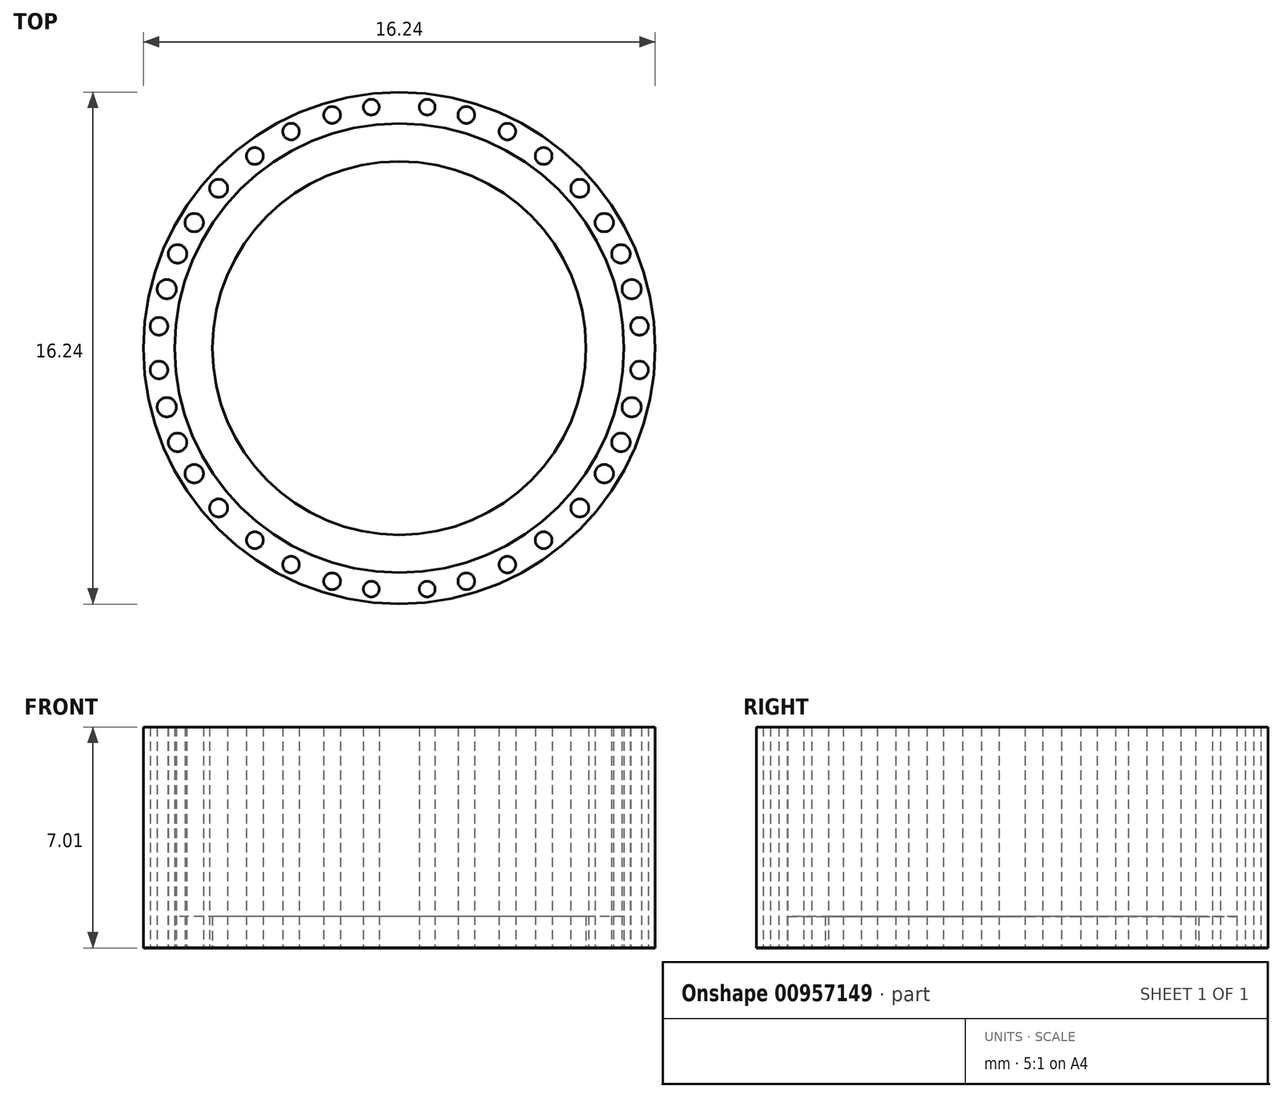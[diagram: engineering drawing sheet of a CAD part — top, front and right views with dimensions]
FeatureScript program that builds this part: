
annotation { "Feature Type Name" : "Feature", "Feature Type Description" : "" }
export const myFeature = defineFeature(function(context is Context, id is Id, definition is map)
    precondition{}
    {
        {
            var Q0;
            Q0=qCreatedBy(makeId("Top.planeOp"),FACE);
            var sketch = newSketch(context, id + "F0", { "sketchPlane" : qUnion([Q0])});
            skCircle(sketch, "E0.0", {"center": v(0, 0) * mm, "radius": 8.22 * mm});
            skCircle(sketch, "E1.0", {"center": v(0, 0) * mm, "radius": 8.12 * mm});
            skCircle(sketch, "E2.0", {"center": v(0, 0) * mm, "radius": 7.13 * mm});
            skCircle(sketch, "E3.0", {"center": v(0, 0) * mm, "radius": 9.1 * mm});
            skCircle(sketch, "E4.0", {"center": v(0, 0) * mm, "radius": 5.93 * mm});
            skSolve(sketch);
        }
        {
            var Q0;
            Q0=makeQuery(id+"F0.imprint","IMPRINT",FACE,{"disambiguationData":[TD([[makeQuery(id+"F0.imprint","IMPRINT",EDGE,{"derivedFrom":sQuery(id+"F0.wireOp",EDGE,"E1.0")}),1.0]])]});
            var Q1;
            Q1=sQuery(id+"F0.wireOp",EDGE,"E1.0");
            var Q2;
            Q2=sQuery(id+"F0.wireOp",EDGE,"E2.0");
            extrude(context, id + "F1", {"entities" : qUnion([Q0]), "surfaceEntities" : qUnion([Q1, Q2]), "depth" : 0.01 * mm, "offsetDistance" : 25 * mm});
        }
        {
            var Q0;
            Q0=makeQuery(id+"F0.imprint","IMPRINT",FACE,{"disambiguationData":[TD([[makeQuery(id+"F0.imprint","IMPRINT",EDGE,{"derivedFrom":sQuery(id+"F0.wireOp",EDGE,"E2.0")}),1.0]])]});
            extrude(context, id + "F2", {"entities" : qUnion([Q0]), "operationType" : NewBodyOperationType.ADD, "depth" : 1 * mm, "offsetDistance" : 25 * mm});
        }
        {
            var Q0;
            Q0=makeQuery(id+"F1.opExtrude","CAP_FACE",FACE,{"disambiguationData":[OSD([sQuery(id+"F0.wireOp",EDGE,"E1.0"),sQuery(id+"F0.wireOp",EDGE,"E2.0")])],"isStart":false});
            var sketch = newSketch(context, id + "F3", { "sketchPlane" : qUnion([Q0])});
            skCircle(sketch, "E5", {"center": v(-4.58, 6.1) * mm, "radius": 0.27 * mm});
            skCircle(sketch, "E6", {"center": v(-5.73, 5.07) * mm, "radius": 0.29 * mm});
            skCircle(sketch, "E7", {"center": v(-6.5, 3.98) * mm, "radius": 0.3 * mm});
            skCircle(sketch, "E8", {"center": v(-7.03, 3) * mm, "radius": 0.3 * mm});
            skCircle(sketch, "E9", {"center": v(-7.37, 1.87) * mm, "radius": 0.3 * mm});
            skCircle(sketch, "E10", {"center": v(-7.62, 0.7) * mm, "radius": 0.28 * mm});
            skCircle(sketch, "E11", {"center": v(-3.43, 6.87) * mm, "radius": 0.26 * mm});
            skCircle(sketch, "E12", {"center": v(-2.13, 7.4) * mm, "radius": 0.27 * mm});
            skCircle(sketch, "E13", {"center": v(-0.89, 7.65) * mm, "radius": 0.25 * mm});
            skCircle(sketch, "E14.MirrorC", {"center": v(6.5, 3.98) * mm, "radius": 0.3 * mm});
            skCircle(sketch, "E15.MirrorC", {"center": v(0.89, 7.65) * mm, "radius": 0.25 * mm});
            skCircle(sketch, "E16.MirrorC", {"center": v(7.03, 3) * mm, "radius": 0.3 * mm});
            skCircle(sketch, "E17.MirrorC", {"center": v(7.62, 0.7) * mm, "radius": 0.28 * mm});
            skCircle(sketch, "E18.MirrorC", {"center": v(7.37, 1.87) * mm, "radius": 0.3 * mm});
            skCircle(sketch, "E19.MirrorC", {"center": v(5.73, 5.07) * mm, "radius": 0.29 * mm});
            skCircle(sketch, "E20.MirrorC", {"center": v(4.58, 6.1) * mm, "radius": 0.27 * mm});
            skCircle(sketch, "E21.MirrorC", {"center": v(3.43, 6.87) * mm, "radius": 0.26 * mm});
            skCircle(sketch, "E22.MirrorC", {"center": v(2.13, 7.4) * mm, "radius": 0.27 * mm});
            skCircle(sketch, "E23.MirrorC", {"center": v(3.43, -6.87) * mm, "radius": 0.26 * mm});
            skCircle(sketch, "E24.MirrorC", {"center": v(2.13, -7.4) * mm, "radius": 0.27 * mm});
            skCircle(sketch, "E25.MirrorC", {"center": v(7.62, -0.7) * mm, "radius": 0.28 * mm});
            skCircle(sketch, "E26.MirrorC", {"center": v(-0.89, -7.65) * mm, "radius": 0.25 * mm});
            skCircle(sketch, "E27.MirrorC", {"center": v(7.37, -1.87) * mm, "radius": 0.3 * mm});
            skCircle(sketch, "E28.MirrorC", {"center": v(0.89, -7.65) * mm, "radius": 0.25 * mm});
            skCircle(sketch, "E29.MirrorC", {"center": v(6.5, -3.98) * mm, "radius": 0.3 * mm});
            skCircle(sketch, "E30.MirrorC", {"center": v(-4.58, -6.1) * mm, "radius": 0.27 * mm});
            skCircle(sketch, "E31.MirrorC", {"center": v(-7.37, -1.87) * mm, "radius": 0.3 * mm});
            skCircle(sketch, "E32.MirrorC", {"center": v(-7.62, -0.7) * mm, "radius": 0.28 * mm});
            skCircle(sketch, "E33.MirrorC", {"center": v(4.58, -6.1) * mm, "radius": 0.27 * mm});
            skCircle(sketch, "E34.MirrorC", {"center": v(-2.13, -7.4) * mm, "radius": 0.27 * mm});
            skCircle(sketch, "E35.MirrorC", {"center": v(-3.43, -6.87) * mm, "radius": 0.26 * mm});
            skCircle(sketch, "E36.MirrorC", {"center": v(5.73, -5.07) * mm, "radius": 0.29 * mm});
            skCircle(sketch, "E37.MirrorC", {"center": v(-5.73, -5.07) * mm, "radius": 0.29 * mm});
            skCircle(sketch, "E38.MirrorC", {"center": v(7.03, -3) * mm, "radius": 0.3 * mm});
            skCircle(sketch, "E39.MirrorC", {"center": v(-6.5, -3.98) * mm, "radius": 0.3 * mm});
            skCircle(sketch, "E40.MirrorC", {"center": v(-7.03, -3) * mm, "radius": 0.3 * mm});
            skSolve(sketch);
        }
        {
            var Q0;
            Q0=makeQuery(id+"F3.imprint","IMPRINT",FACE,{"disambiguationData":[TD([[makeQuery(id+"F3.imprint","IMPRINT",EDGE,{"derivedFrom":sQuery(id+"F3.wireOp",EDGE,"E11")}),-1.0]])]});
            var Q1;
            Q1=sQuery(id+"F3.wireOp",EDGE,"E11");
            var Q2;
            Q2=sQuery(id+"F3.wireOp",EDGE,"E34.MirrorC");
            var Q3;
            Q3=sQuery(id+"F3.wireOp",EDGE,"E24.MirrorC");
            var Q4;
            Q4=sQuery(id+"F3.wireOp",EDGE,"E39.MirrorC");
            var Q5;
            Q5=sQuery(id+"F3.wireOp",EDGE,"E6");
            var Q6;
            Q6=sQuery(id+"F3.wireOp",EDGE,"E8");
            var Q7;
            Q7=sQuery(id+"F3.wireOp",EDGE,"E28.MirrorC");
            var Q8;
            Q8=sQuery(id+"F3.wireOp",EDGE,"E5");
            var Q9;
            Q9=sQuery(id+"F3.wireOp",EDGE,"E32.MirrorC");
            var Q10;
            Q10=sQuery(id+"F3.wireOp",EDGE,"E30.MirrorC");
            var Q11;
            Q11=sQuery(id+"F3.wireOp",EDGE,"E40.MirrorC");
            var Q12;
            Q12=sQuery(id+"F3.wireOp",EDGE,"E25.MirrorC");
            var Q13;
            Q13=sQuery(id+"F3.wireOp",EDGE,"E19.MirrorC");
            var Q14;
            Q14=sQuery(id+"F3.wireOp",EDGE,"E15.MirrorC");
            var Q15;
            Q15=sQuery(id+"F3.wireOp",EDGE,"E36.MirrorC");
            var Q16;
            Q16=sQuery(id+"F3.wireOp",EDGE,"E33.MirrorC");
            var Q17;
            Q17=sQuery(id+"F3.wireOp",EDGE,"E26.MirrorC");
            var Q18;
            Q18=sQuery(id+"F3.wireOp",EDGE,"E38.MirrorC");
            var Q19;
            Q19=sQuery(id+"F3.wireOp",EDGE,"E7");
            var Q20;
            Q20=sQuery(id+"F3.wireOp",EDGE,"E17.MirrorC");
            var Q21;
            Q21=sQuery(id+"F3.wireOp",EDGE,"E18.MirrorC");
            var Q22;
            Q22=sQuery(id+"F3.wireOp",EDGE,"E29.MirrorC");
            var Q23;
            Q23=sQuery(id+"F3.wireOp",EDGE,"E27.MirrorC");
            var Q24;
            Q24=sQuery(id+"F3.wireOp",EDGE,"E16.MirrorC");
            var Q25;
            Q25=sQuery(id+"F3.wireOp",EDGE,"E14.MirrorC");
            var Q26;
            Q26=sQuery(id+"F3.wireOp",EDGE,"E35.MirrorC");
            var Q27;
            Q27=sQuery(id+"F3.wireOp",EDGE,"E21.MirrorC");
            var Q28;
            Q28=sQuery(id+"F3.wireOp",EDGE,"E13");
            var Q29;
            Q29=sQuery(id+"F3.wireOp",EDGE,"E22.MirrorC");
            var Q30;
            Q30=sQuery(id+"F3.wireOp",EDGE,"E9");
            var Q31;
            Q31=sQuery(id+"F3.wireOp",EDGE,"E12");
            var Q32;
            Q32=sQuery(id+"F3.wireOp",EDGE,"E37.MirrorC");
            var Q33;
            Q33=sQuery(id+"F3.wireOp",EDGE,"E20.MirrorC");
            var Q34;
            Q34=sQuery(id+"F3.wireOp",EDGE,"E31.MirrorC");
            var Q35;
            Q35=sQuery(id+"F3.wireOp",EDGE,"E10");
            var Q36;
            Q36=sQuery(id+"F3.wireOp",EDGE,"E23.MirrorC");
            var Q37;
            Q37=sQuery(id+"F3.wireOp",EDGE,"E28.MirrorC");
            var Q38;
            Q38=sQuery(id+"F3.wireOp",EDGE,"E5");
            var Q39;
            Q39=sQuery(id+"F3.wireOp",EDGE,"E7");
            var Q40;
            Q40=sQuery(id+"F3.wireOp",EDGE,"E9");
            var Q41;
            Q41=sQuery(id+"F3.wireOp",EDGE,"E11");
            var Q42;
            Q42=sQuery(id+"F3.wireOp",EDGE,"E24.MirrorC");
            var Q43;
            Q43=sQuery(id+"F3.wireOp",EDGE,"E31.MirrorC");
            var Q44;
            Q44=sQuery(id+"F3.wireOp",EDGE,"E16.MirrorC");
            var Q45;
            Q45=sQuery(id+"F3.wireOp",EDGE,"E20.MirrorC");
            var Q46;
            Q46=sQuery(id+"F3.wireOp",EDGE,"E36.MirrorC");
            var Q47;
            Q47=sQuery(id+"F3.wireOp",EDGE,"E17.MirrorC");
            var Q48;
            Q48=sQuery(id+"F3.wireOp",EDGE,"E10");
            var Q49;
            Q49=sQuery(id+"F3.wireOp",EDGE,"E13");
            var Q50;
            Q50=sQuery(id+"F3.wireOp",EDGE,"E22.MirrorC");
            var Q51;
            Q51=sQuery(id+"F3.wireOp",EDGE,"E34.MirrorC");
            var Q52;
            Q52=sQuery(id+"F3.wireOp",EDGE,"E37.MirrorC");
            var Q53;
            Q53=sQuery(id+"F3.wireOp",EDGE,"E29.MirrorC");
            var Q54;
            Q54=sQuery(id+"F3.wireOp",EDGE,"E32.MirrorC");
            var Q55;
            Q55=sQuery(id+"F3.wireOp",EDGE,"E6");
            var Q56;
            Q56=sQuery(id+"F3.wireOp",EDGE,"E40.MirrorC");
            var Q57;
            Q57=sQuery(id+"F3.wireOp",EDGE,"E15.MirrorC");
            var Q58;
            Q58=sQuery(id+"F3.wireOp",EDGE,"E26.MirrorC");
            var Q59;
            Q59=sQuery(id+"F3.wireOp",EDGE,"E35.MirrorC");
            var Q60;
            Q60=sQuery(id+"F3.wireOp",EDGE,"E14.MirrorC");
            var Q61;
            Q61=sQuery(id+"F3.wireOp",EDGE,"E39.MirrorC");
            var Q62;
            Q62=sQuery(id+"F3.wireOp",EDGE,"E21.MirrorC");
            var Q63;
            Q63=sQuery(id+"F3.wireOp",EDGE,"E27.MirrorC");
            var Q64;
            Q64=sQuery(id+"F3.wireOp",EDGE,"E8");
            var Q65;
            Q65=sQuery(id+"F3.wireOp",EDGE,"E18.MirrorC");
            var Q66;
            Q66=sQuery(id+"F3.wireOp",EDGE,"E33.MirrorC");
            var Q67;
            Q67=sQuery(id+"F3.wireOp",EDGE,"E38.MirrorC");
            var Q68;
            Q68=sQuery(id+"F3.wireOp",EDGE,"E19.MirrorC");
            var Q69;
            Q69=sQuery(id+"F3.wireOp",EDGE,"E30.MirrorC");
            var Q70;
            Q70=sQuery(id+"F3.wireOp",EDGE,"E23.MirrorC");
            var Q71;
            Q71=sQuery(id+"F3.wireOp",EDGE,"E25.MirrorC");
            var Q72;
            Q72=sQuery(id+"F3.wireOp",EDGE,"E12");
            extrude(context, id + "F4", {"entities" : qUnion([Q0]), "surfaceEntities" : qUnion([Q1, Q2, Q3, Q4, Q5, Q6, Q7, Q8, Q9, Q10, Q11, Q12, Q13, Q14, Q15, Q16, Q17, Q18, Q19, Q20, Q21, Q22, Q23, Q24, Q25, Q26, Q27, Q28, Q29, Q30, Q31, Q32, Q33, Q34, Q35, Q36, Q37, Q38, Q39, Q40, Q41, Q42, Q43, Q44, Q45, Q46, Q47, Q48, Q49, Q50, Q51, Q52, Q53, Q54, Q55, Q56, Q57, Q58, Q59, Q60, Q61, Q62, Q63, Q64, Q65, Q66, Q67, Q68, Q69, Q70, Q71, Q72]), "depth" : 7 * mm, "offsetDistance" : 25 * mm});
        }
        {
            var Q0;
            Q0=makeQuery(id+"F1.opExtrude","SWEPT_BODY",BODY,{"disambiguationData":[OSD([sQuery(id+"F0.wireOp",EDGE,"E1.0"),sQuery(id+"F0.wireOp",EDGE,"E2.0")])]});
            transform(context, id + "F5", {"entities" : qUnion([Q0]), "transformType" : TransformType.TRANSLATION_3D, "dx" : 0 * mm, "dy" : 0 * mm, "dz" : 5.9 * mm, "makeCopy" : false});
        }
        {
            var Q0;
            {var subQ0=sQuery(id+"F0.wireOp",EDGE,"E2.0");Q0=makeQuery(id+"F2.boolean.opBoolean","MERGE",BODY,{"derivedFrom":[makeQuery(id+"F1.opExtrude","SWEPT_BODY",BODY,{"disambiguationData":[OSD([sQuery(id+"F0.wireOp",EDGE,"E1.0"),subQ0])]}),makeQuery(id+"F2.opExtrude","SWEPT_BODY",BODY,{"disambiguationData":[OSD([subQ0,sQuery(id+"F0.wireOp",EDGE,"E4.0")])]})]});}
            transform(context, id + "F6", {"entities" : qUnion([Q0]), "transformType" : TransformType.TRANSLATION_3D, "dx" : 0 * mm, "dy" : 0 * mm, "dz" : -5.9 * mm, "makeCopy" : false});
        }
    });
